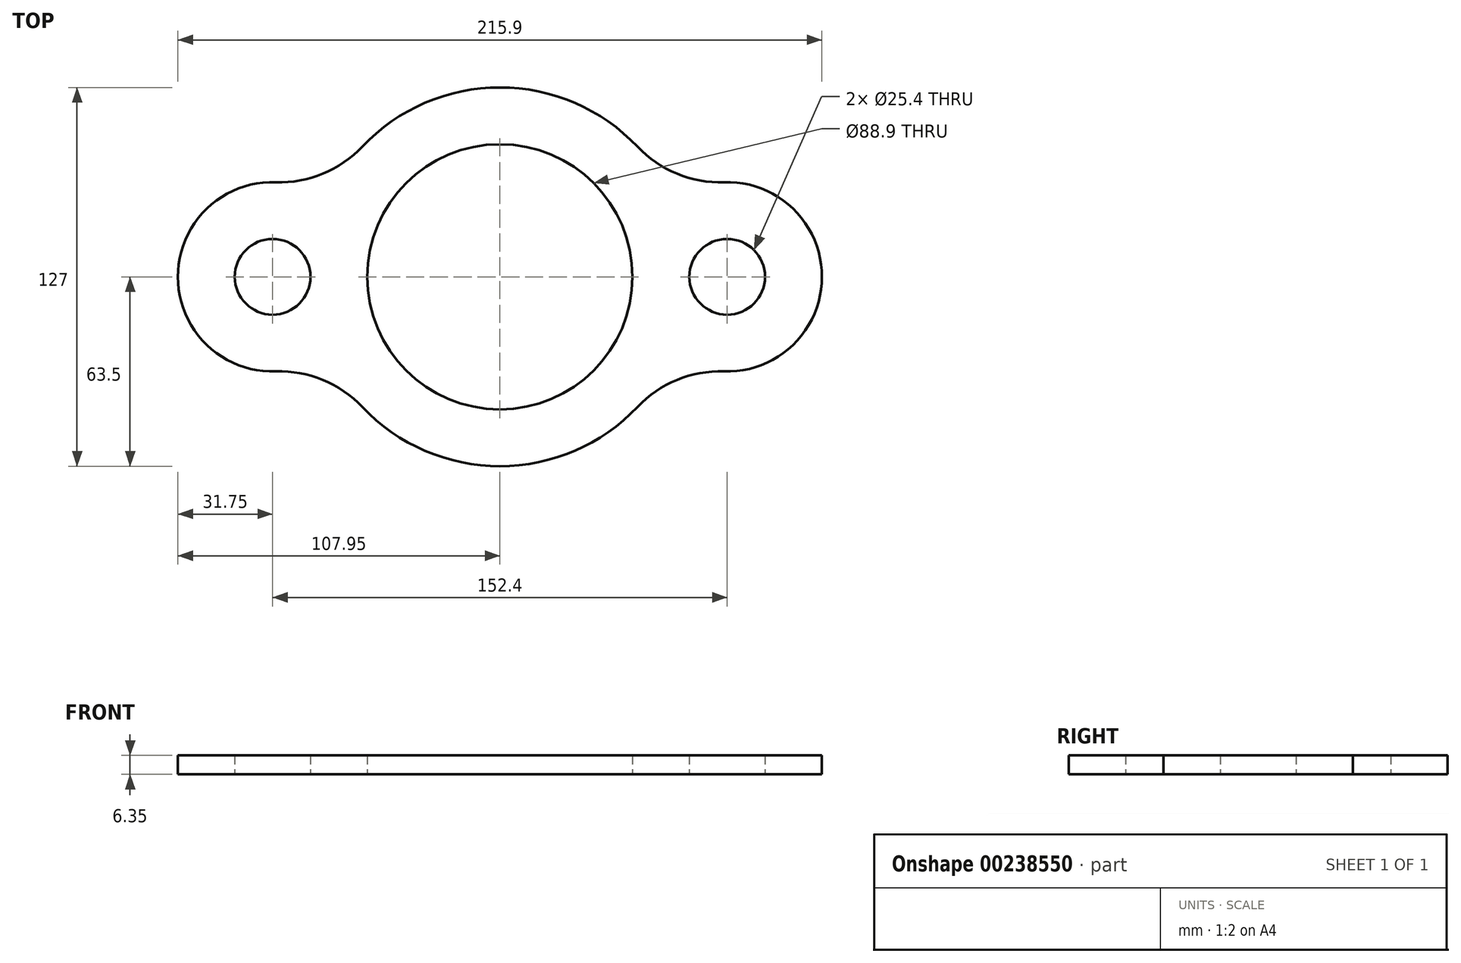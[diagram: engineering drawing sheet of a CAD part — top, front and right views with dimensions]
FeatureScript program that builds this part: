
annotation { "Feature Type Name" : "Feature", "Feature Type Description" : "" }
export const myFeature = defineFeature(function(context is Context, id is Id, definition is map)
    precondition{}
    {
        {
            var Q0;
            Q0=qCreatedBy(makeId("Top.planeOp"),FACE);
            var sketch = newSketch(context, id + "F0", { "sketchPlane" : qUnion([Q0])});
            skCircle(sketch, "E0", {"center": v(0, 0) * mm, "radius": 44.45 * mm});
            skLineSegment(sketch, "E1", {"start": v(0, 0) * mm, "end": v(-76.2, 0) * mm});
            skLineSegment(sketch, "E2", {"start": v(0, 0) * mm, "end": v(76.2, 0) * mm});
            skLineSegment(sketch, "E3", {"start": v(-53.35, 0) * mm, "end": v(57.8, 0) * mm});
            skCircle(sketch, "E4", {"center": v(-76.2, 0) * mm, "radius": 12.7 * mm});
            skCircle(sketch, "E5", {"center": v(76.2, 0) * mm, "radius": 12.7 * mm});
            skArc(sketch, "E6", {"start": v(46.14, 43.63) * mm, "mid": v(0, 63.5) * mm, "end": v(-46.14, 43.63) * mm});
            skArc(sketch, "E7", {"start": v(-75.12, 31.73) * mm, "mid": v(-107.95, 0) * mm, "end": v(-75.12, -31.73) * mm});
            skArc(sketch, "E8", {"start": v(75.12, -31.73) * mm, "mid": v(107.95, 0) * mm, "end": v(75.12, 31.73) * mm});
            skArc(sketch, "E9.trimOffspring", {"start": v(-46.14, -43.63) * mm, "mid": v(0, -63.5) * mm, "end": v(46.14, -43.63) * mm});
            skPoint(sketch, "E10.visualSharp", {"position": v(-57.94, 25.98) * mm});
            skArc(sketch, "E10.filletArc", {"start": v(-75.12, 31.73) * mm, "mid": v(-59.35, 34.56) * mm, "end": v(-46.14, 43.63) * mm});
            skPoint(sketch, "E11.visualSharp", {"position": v(-57.94, -25.98) * mm});
            skArc(sketch, "E11.filletArc", {"start": v(-46.14, -43.63) * mm, "mid": v(-59.35, -34.56) * mm, "end": v(-75.12, -31.73) * mm});
            skPoint(sketch, "E12.visualSharp", {"position": v(57.94, -25.98) * mm});
            skArc(sketch, "E12.filletArc", {"start": v(75.12, -31.73) * mm, "mid": v(59.35, -34.56) * mm, "end": v(46.14, -43.63) * mm});
            skPoint(sketch, "E13.visualSharp", {"position": v(57.94, 25.98) * mm});
            skArc(sketch, "E13.filletArc", {"start": v(46.14, 43.63) * mm, "mid": v(59.35, 34.56) * mm, "end": v(75.12, 31.73) * mm});
            skArc(sketch, "E14.MirrorCS", {"start": v(75.12, 31.73) * mm, "mid": v(59.35, 34.56) * mm, "end": v(46.14, 43.63) * mm});
            skArc(sketch, "E15.MirrorCS", {"start": v(46.14, -43.63) * mm, "mid": v(59.35, -34.56) * mm, "end": v(75.12, -31.73) * mm});
            skSolve(sketch);
        }
        {
            var Q0;
            Q0 = qSketchRegion(id + "F0", true);
            extrude(context, id + "F1", {"entities" : qUnion([Q0]), "depth" : 6.35 * mm});
        }
    });
